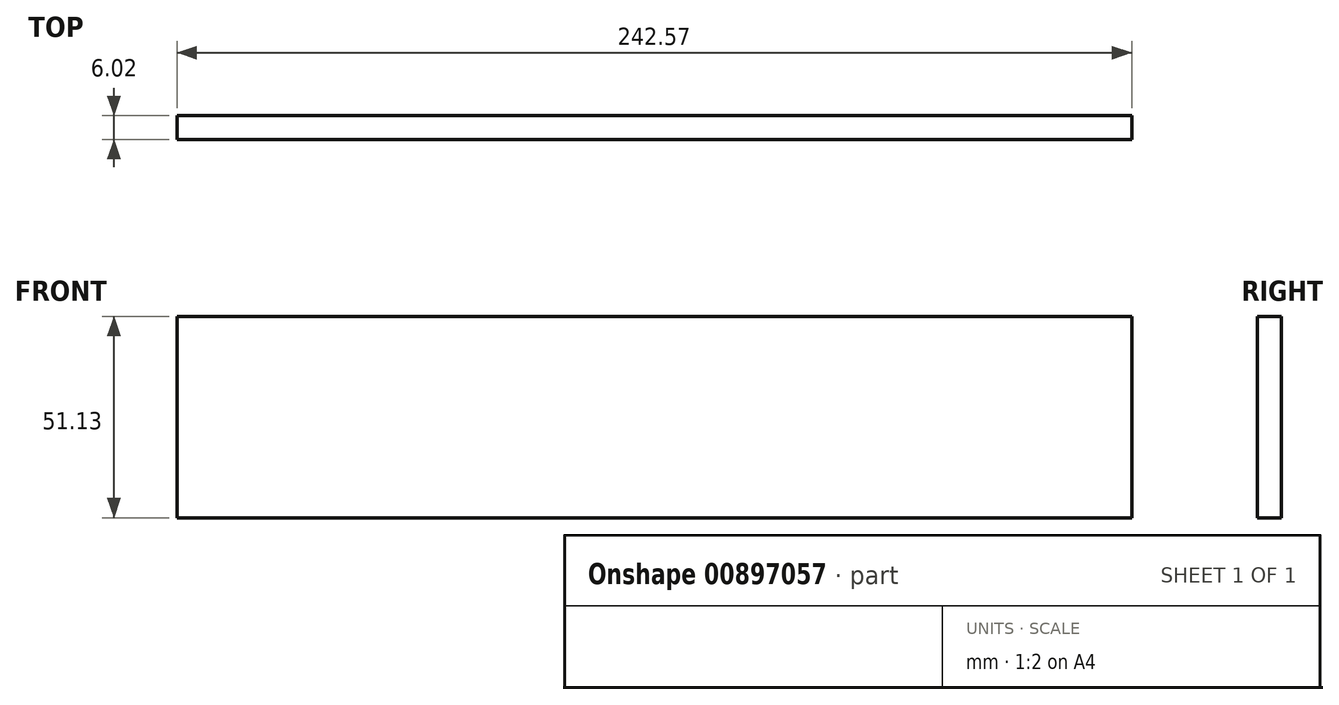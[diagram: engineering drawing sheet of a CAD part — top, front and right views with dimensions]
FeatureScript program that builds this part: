
annotation { "Feature Type Name" : "Feature", "Feature Type Description" : "" }
export const myFeature = defineFeature(function(context is Context, id is Id, definition is map)
    precondition{}
    {
        {
            var Q0;
            Q0=qCreatedBy(makeId("Front.planeOp"),FACE);
            var sketch = newSketch(context, id + "F0", { "sketchPlane" : qUnion([Q0])});
            skLineSegment(sketch, "E0.bottom", {"start": v(0, 0) * mm, "end": v(242.57, 0) * mm});
            skLineSegment(sketch, "E0.top", {"start": v(0, 51.13) * mm, "end": v(242.57, 51.13) * mm});
            skLineSegment(sketch, "E0.left", {"start": v(0, 0) * mm, "end": v(0, 51.13) * mm});
            skLineSegment(sketch, "E0.right", {"start": v(242.57, 0) * mm, "end": v(242.57, 51.13) * mm});
            skSolve(sketch);
        }
        {
            var Q0;
            Q0 = qSketchRegion(id + "F0", true);
            extrude(context, id + "F1", {"entities" : qUnion([Q0]), "depth" : 6.02 * mm, "offsetDistance" : 25.4 * mm});
        }
    });
